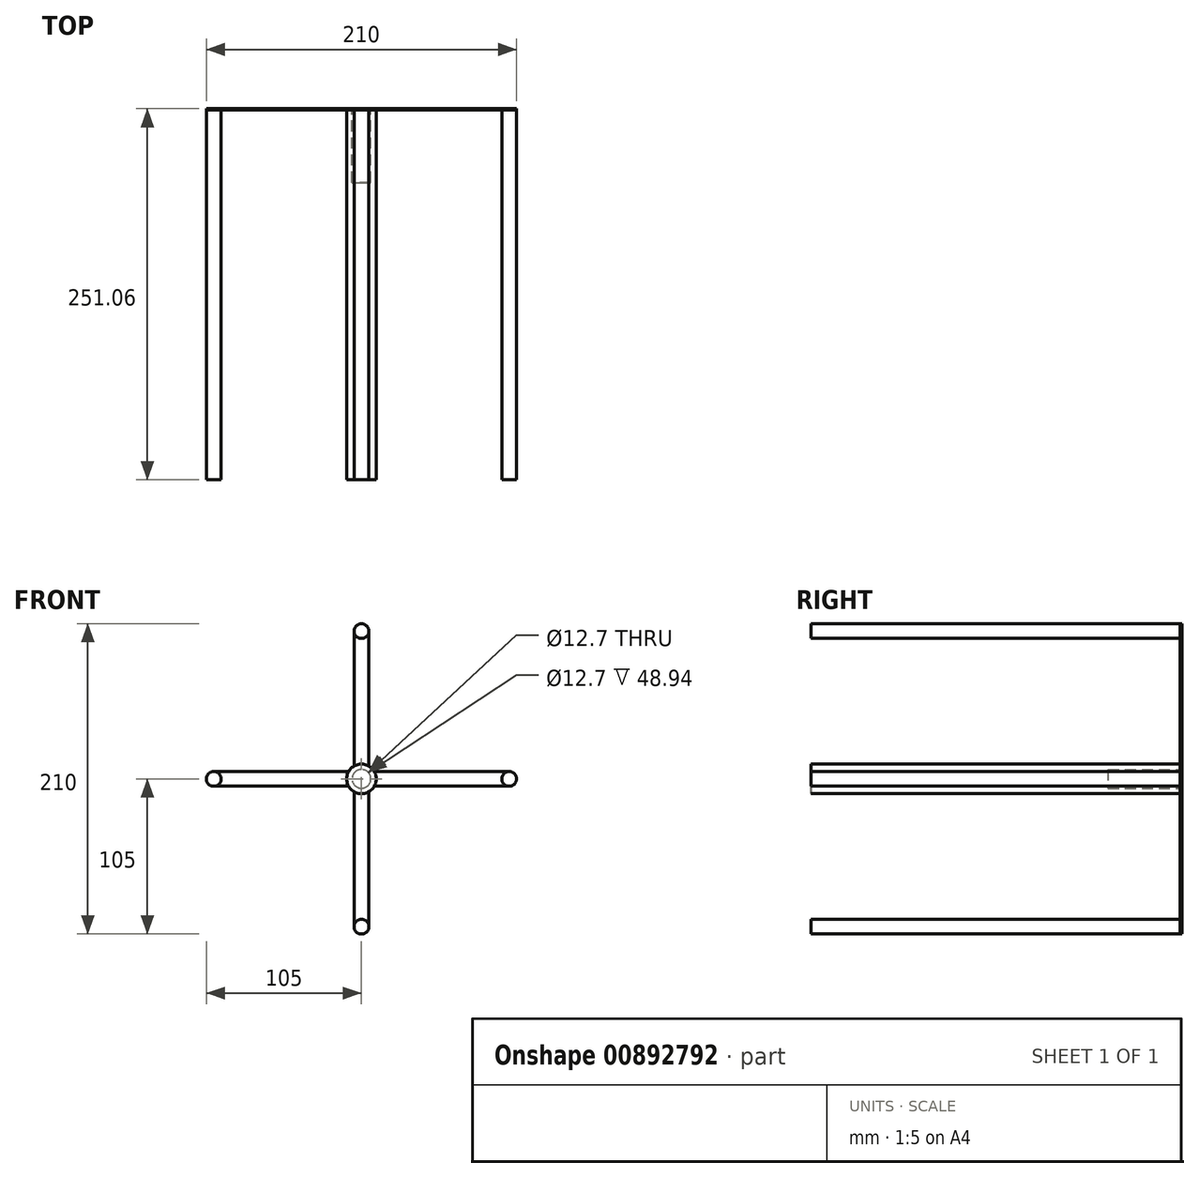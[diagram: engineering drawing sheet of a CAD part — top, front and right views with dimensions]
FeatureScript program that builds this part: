
annotation { "Feature Type Name" : "Feature", "Feature Type Description" : "" }
export const myFeature = defineFeature(function(context is Context, id is Id, definition is map)
    precondition{}
    {
        {
            var Q0;
            Q0=qCreatedBy(makeId("Front.planeOp"),FACE);
            var sketch = newSketch(context, id + "F0", { "sketchPlane" : qUnion([Q0])});
            skLineSegment(sketch, "E0", {"start": v(-100, 0) * mm, "end": v(0, 0) * mm, "construction": true});
            skLineSegment(sketch, "E1", {"start": v(0, 0) * mm, "end": v(100, 0) * mm, "construction": true});
            skLineSegment(sketch, "E2", {"start": v(0, 100) * mm, "end": v(0, 0) * mm, "construction": true});
            skLineSegment(sketch, "E3", {"start": v(0, -100) * mm, "end": v(0, 0) * mm, "construction": true});
            skCircle(sketch, "E4", {"center": v(0, 0) * mm, "radius": 10 * mm});
            skCircle(sketch, "E5", {"center": v(0, 100) * mm, "radius": 5 * mm});
            skCircle(sketch, "E6", {"center": v(-100, 0) * mm, "radius": 5 * mm});
            skCircle(sketch, "E7", {"center": v(0, -100) * mm, "radius": 5 * mm});
            skCircle(sketch, "E8", {"center": v(100, 0) * mm, "radius": 5 * mm});
            skSolve(sketch);
        }
        {
            var Q0;
            Q0=makeQuery(id+"F0.imprint","IMPRINT",FACE,{"disambiguationData":[TD([[makeQuery(id+"F0.imprint","IMPRINT",EDGE,{"derivedFrom":sQuery(id+"F0.wireOp",EDGE,"E4")}),1.0]])]});
            var Q1;
            Q1=makeQuery(id+"F0.imprint","IMPRINT",FACE,{"disambiguationData":[TD([[makeQuery(id+"F0.imprint","IMPRINT",EDGE,{"derivedFrom":sQuery(id+"F0.wireOp",EDGE,"E6")}),1.0]])]});
            var Q2;
            Q2=makeQuery(id+"F0.imprint","IMPRINT",FACE,{"disambiguationData":[TD([[makeQuery(id+"F0.imprint","IMPRINT",EDGE,{"derivedFrom":sQuery(id+"F0.wireOp",EDGE,"E7")}),1.0]])]});
            var Q3;
            Q3=makeQuery(id+"F0.imprint","IMPRINT",FACE,{"disambiguationData":[TD([[makeQuery(id+"F0.imprint","IMPRINT",EDGE,{"derivedFrom":sQuery(id+"F0.wireOp",EDGE,"E8")}),1.0]])]});
            var Q4;
            Q4=makeQuery(id+"F0.imprint","IMPRINT",FACE,{"disambiguationData":[TD([[makeQuery(id+"F0.imprint","IMPRINT",EDGE,{"derivedFrom":sQuery(id+"F0.wireOp",EDGE,"E5")}),1.0]])]});
            extrude(context, id + "F1", {"entities" : qUnion([Q0, Q1, Q2, Q3, Q4]), "depth" : 250 * mm, "offsetDistance" : 25 * mm});
        }
        {
            var Q0;
            Q0=makeQuery(id+"F1.opExtrude","CAP_FACE",FACE,{"disambiguationData":[OSD([sQuery(id+"F0.wireOp",EDGE,"E4")])],"isStart":true});
            var sketch = newSketch(context, id + "F2", { "sketchPlane" : qUnion([Q0])});
            skCircle(sketch, "E9.0", {"center": v(0, 0) * mm, "radius": 10 * mm});
            skCircle(sketch, "E10.0", {"center": v(0, -100) * mm, "radius": 5 * mm});
            skCircle(sketch, "E10.1", {"center": v(100, 0) * mm, "radius": 5 * mm});
            skCircle(sketch, "E10.2", {"center": v(-100, 0) * mm, "radius": 5 * mm});
            skCircle(sketch, "E10.3", {"center": v(0, 100) * mm, "radius": 5 * mm});
            skLineSegment(sketch, "E11", {"start": v(0, 0) * mm, "end": v(0, 0) * mm});
            skLineSegment(sketch, "E12", {"start": v(0, -9.1) * mm, "end": v(0, -9.1) * mm});
            skLineSegment(sketch, "E13", {"start": v(0, 0) * mm, "end": v(0, 100) * mm, "construction": true});
            skLineSegment(sketch, "E14", {"start": v(0, 0) * mm, "end": v(100, 0) * mm, "construction": true});
            skLineSegment(sketch, "E15", {"start": v(0, 0) * mm, "end": v(0, -100) * mm, "construction": true});
            skLineSegment(sketch, "E16", {"start": v(-100, 0) * mm, "end": v(0, 0) * mm, "construction": true});
            skLineSegment(sketch, "E17", {"start": v(8.66, -5) * mm, "end": v(100, -5) * mm});
            skLineSegment(sketch, "E18", {"start": v(100, -5) * mm, "end": v(8.66, -5) * mm});
            skLineSegment(sketch, "E19", {"start": v(100, 5) * mm, "end": v(8.66, 5) * mm});
            skLineSegment(sketch, "E20.MirrorCS", {"start": v(-8.66, -5) * mm, "end": v(-100, -5) * mm});
            skLineSegment(sketch, "E21.MirrorCS", {"start": v(-100, 5) * mm, "end": v(-8.66, 5) * mm});
            skLineSegment(sketch, "E22", {"start": v(5, -8.66) * mm, "end": v(5, -100) * mm});
            skLineSegment(sketch, "E23", {"start": v(-5, -8.66) * mm, "end": v(-5, -100) * mm});
            skLineSegment(sketch, "E24.MirrorCS", {"start": v(5, 8.66) * mm, "end": v(5, 100) * mm});
            skLineSegment(sketch, "E25.MirrorCS", {"start": v(-5, 8.66) * mm, "end": v(-5, 100) * mm});
            skSolve(sketch);
        }
        {
            var Q0;
            Q0 = qSketchRegion(id + "F2", true);
            extrude(context, id + "F3", {"entities" : qUnion([Q0]), "depth" : 1.06 * mm, "offsetDistance" : 25 * mm});
        }
        {
            var Q0;
            Q0=makeQuery(id+"F3.opExtrude","CAP_FACE",FACE,{"disambiguationData":[OSD([sQuery(id+"F2.wireOp",EDGE,"E9.0"),sQuery(id+"F2.wireOp",EDGE,"E10.0"),sQuery(id+"F2.wireOp",EDGE,"E10.1"),sQuery(id+"F2.wireOp",EDGE,"E10.2"),sQuery(id+"F2.wireOp",EDGE,"E10.3"),sQuery(id+"F2.wireOp",EDGE,"E18"),sQuery(id+"F2.wireOp",EDGE,"E19"),sQuery(id+"F2.wireOp",EDGE,"E20.MirrorCS"),sQuery(id+"F2.wireOp",EDGE,"E21.MirrorCS"),sQuery(id+"F2.wireOp",EDGE,"E22"),sQuery(id+"F2.wireOp",EDGE,"E23"),sQuery(id+"F2.wireOp",EDGE,"E24.MirrorCS"),sQuery(id+"F2.wireOp",EDGE,"E25.MirrorCS")])],"isStart":false});
            var sketch = newSketch(context, id + "F4", { "sketchPlane" : qUnion([Q0])});
            skPoint(sketch, "E26.0", {"position": v(8.66, -5) * mm});
            skArc(sketch, "E27.0", {"start": v(8.66, -5) * mm, "mid": v(7.07, -7.07) * mm, "end": v(5, -8.66) * mm});
            skArc(sketch, "E28.0", {"start": v(5, 8.66) * mm, "mid": v(7.07, 7.07) * mm, "end": v(8.66, 5) * mm});
            skArc(sketch, "E29.0", {"start": v(-5, -8.66) * mm, "mid": v(-7.07, -7.07) * mm, "end": v(-8.66, -5) * mm});
            skCircle(sketch, "E30", {"center": v(0, 0) * mm, "radius": 10 * mm, "construction": true});
            skPoint(sketch, "E30.first.point", {"position": v(7.07, -7.07) * mm});
            skPoint(sketch, "E30.second.point", {"position": v(-7.07, -7.07) * mm});
            skPoint(sketch, "E30.third.point", {"position": v(7.07, 7.07) * mm});
            skCircle(sketch, "E31", {"center": v(0, 0) * mm, "radius": 6.35 * mm});
            skSolve(sketch);
        }
        {
            var Q0;
            Q0 = qSketchRegion(id + "F4", true);
            extrude(context, id + "F5", {"entities" : qUnion([Q0]), "operationType" : NewBodyOperationType.REMOVE, "oppositeDirection" : true, "depth" : 50 * mm, "offsetDistance" : 25 * mm});
        }
    });
